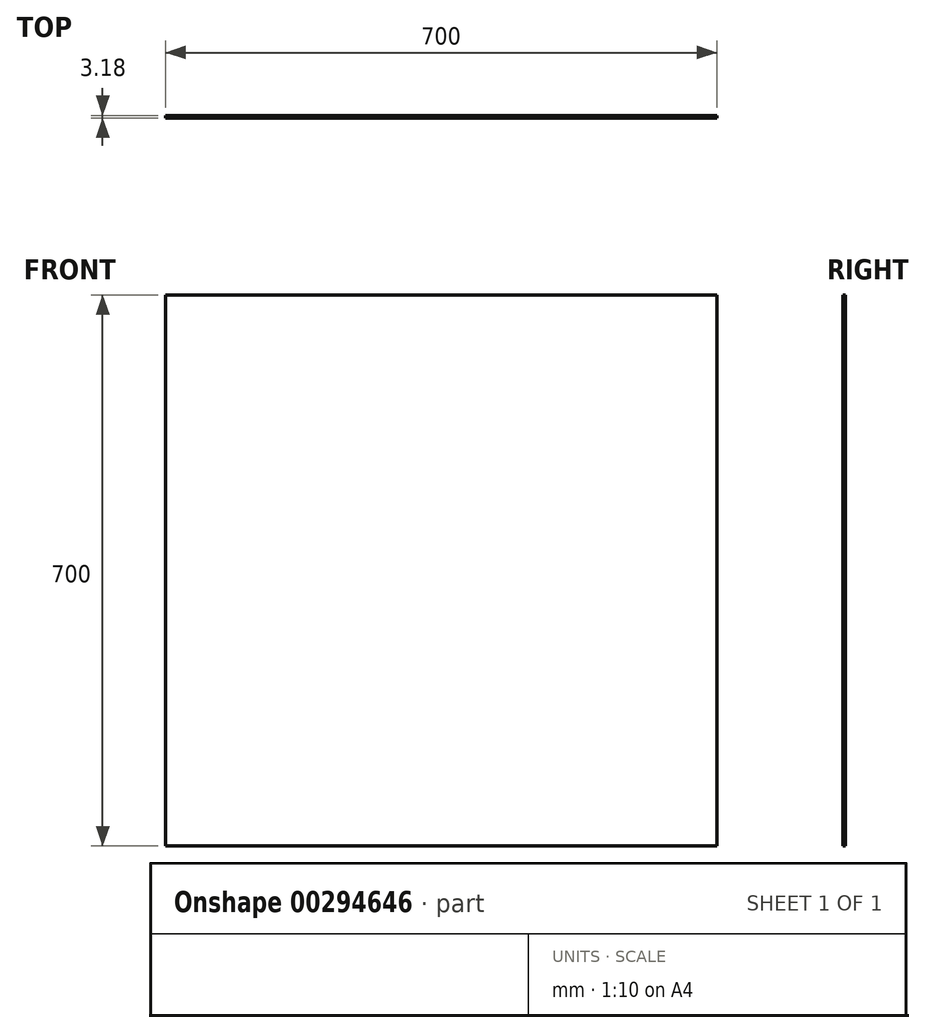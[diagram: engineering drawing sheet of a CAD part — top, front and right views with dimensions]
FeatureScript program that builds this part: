
annotation { "Feature Type Name" : "Feature", "Feature Type Description" : "" }
export const myFeature = defineFeature(function(context is Context, id is Id, definition is map)
    precondition{}
    {
        {
            var Q0;
            Q0=qCreatedBy(makeId("Front.planeOp"),FACE);
            var sketch = newSketch(context, id + "F0", { "sketchPlane" : qUnion([Q0])});
            skLineSegment(sketch, "E0.bottom", {"start": v(350, 350) * mm, "end": v(-350, 350) * mm});
            skLineSegment(sketch, "E0.top", {"start": v(350, -350) * mm, "end": v(-350, -350) * mm});
            skLineSegment(sketch, "E0.left", {"start": v(350, 350) * mm, "end": v(350, -350) * mm});
            skLineSegment(sketch, "E0.right", {"start": v(-350, 350) * mm, "end": v(-350, -350) * mm});
            skPoint(sketch, "E0.middle", {"position": v(0, 0) * mm});
            skSolve(sketch);
        }
        {
            var Q0;
            Q0 = qSketchRegion(id + "F0", true);
            extrude(context, id + "F1", {"entities" : qUnion([Q0]), "endBound" : BoundingType.SYMMETRIC, "depth" : 3.17 * mm});
        }
    });
